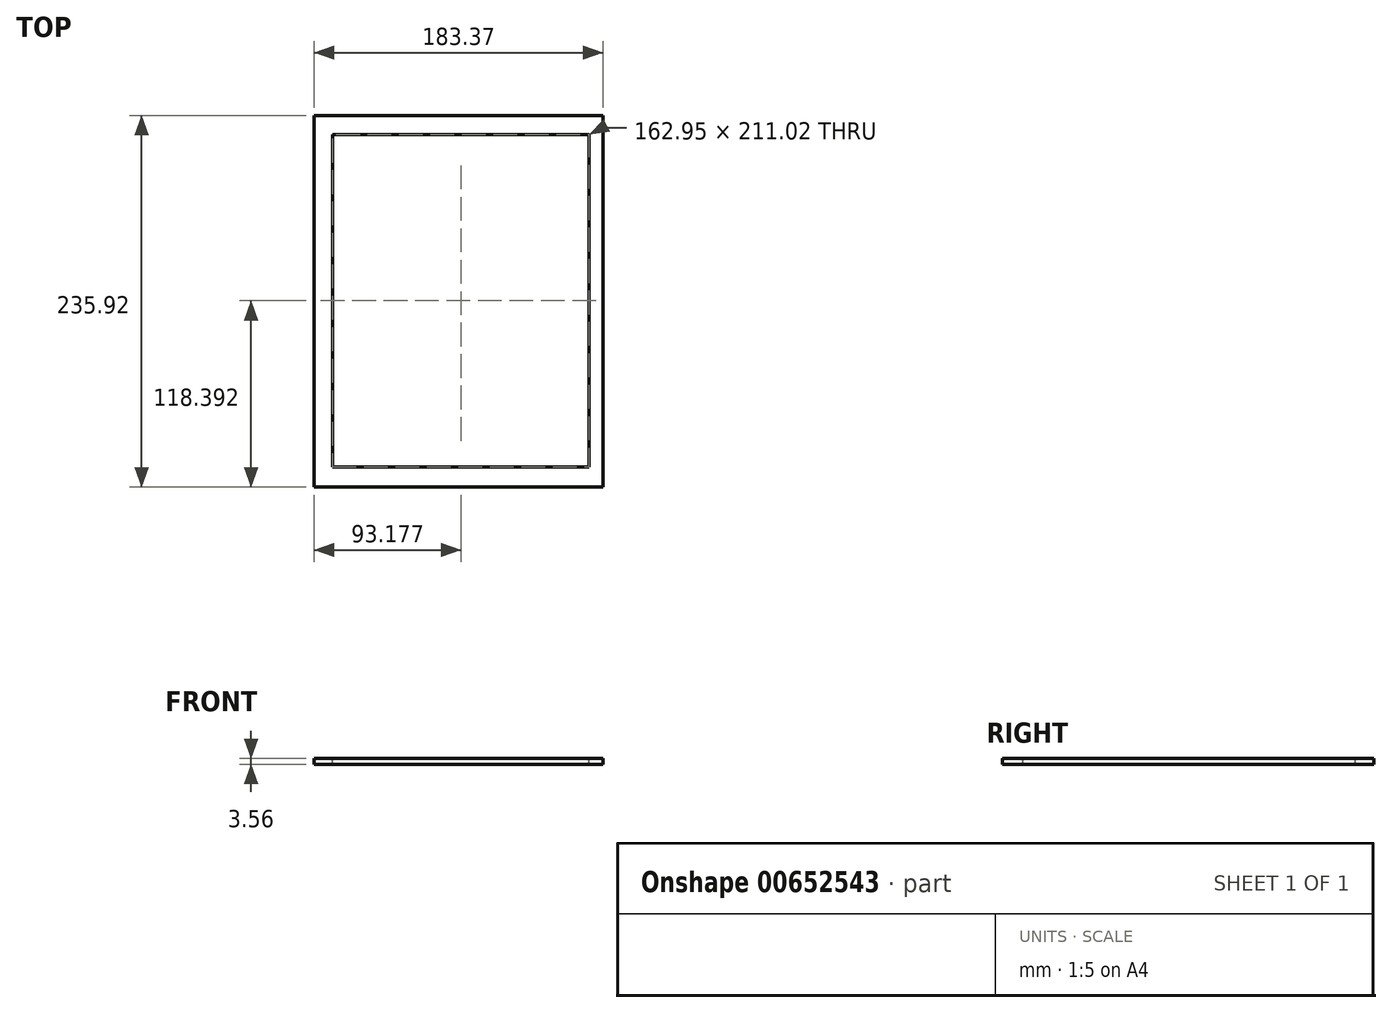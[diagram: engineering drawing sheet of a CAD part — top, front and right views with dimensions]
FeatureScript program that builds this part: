
annotation { "Feature Type Name" : "Feature", "Feature Type Description" : "" }
export const myFeature = defineFeature(function(context is Context, id is Id, definition is map)
    precondition{}
    {
        {
            var Q0;
            Q0=qCreatedBy(makeId("Top.planeOp"),FACE);
            var sketch = newSketch(context, id + "F0", { "sketchPlane" : qUnion([Q0])});
            skLineSegment(sketch, "E0.bottom", {"start": v(-86.94, 111.9) * mm, "end": v(96.43, 111.9) * mm});
            skLineSegment(sketch, "E0.top", {"start": v(-86.94, -124.02) * mm, "end": v(96.43, -124.02) * mm});
            skLineSegment(sketch, "E0.left", {"start": v(-86.94, 111.9) * mm, "end": v(-86.94, -124.02) * mm});
            skLineSegment(sketch, "E0.right", {"start": v(96.43, 111.9) * mm, "end": v(96.43, -124.02) * mm});
            skLineSegment(sketch, "E1.bottom", {"start": v(-75.24, 99.88) * mm, "end": v(87.71, 99.88) * mm});
            skLineSegment(sketch, "E1.top", {"start": v(-75.24, -111.14) * mm, "end": v(87.71, -111.14) * mm});
            skLineSegment(sketch, "E1.left", {"start": v(-75.24, 99.88) * mm, "end": v(-75.24, -111.14) * mm});
            skLineSegment(sketch, "E1.right", {"start": v(87.71, 99.88) * mm, "end": v(87.71, -111.14) * mm});
            skSolve(sketch);
        }
        {
            var Q0;
            Q0=makeQuery(id+"F0.imprint","IMPRINT",FACE,{"disambiguationData":[TD([[makeQuery(id+"F0.imprint","IMPRINT",EDGE,{"derivedFrom":sQuery(id+"F0.wireOp",EDGE,"E0.bottom")}),-1.0]])]});
            extrude(context, id + "F1", {"entities" : qUnion([Q0]), "oppositeDirection" : true, "depth" : 3.56 * mm, "offsetDistance" : 25.4 * mm});
        }
    });
